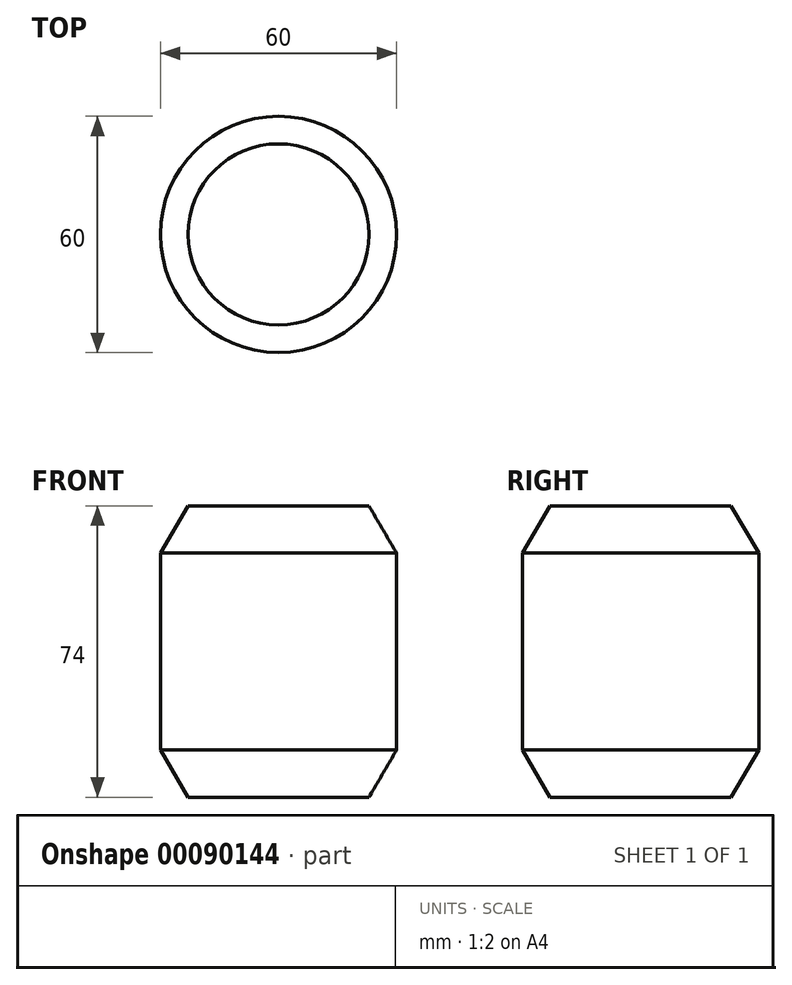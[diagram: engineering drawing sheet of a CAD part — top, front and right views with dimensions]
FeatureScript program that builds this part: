
annotation { "Feature Type Name" : "Feature", "Feature Type Description" : "" }
export const myFeature = defineFeature(function(context is Context, id is Id, definition is map)
    precondition{}
    {
        {
            var Q0;
            Q0=qCreatedBy(makeId("Top.planeOp"),FACE);
            var sketch = newSketch(context, id + "F0", { "sketchPlane" : qUnion([Q0])});
            skCircle(sketch, "E0", {"center": v(0, 0) * mm, "radius": 30 * mm});
            skCircle(sketch, "E1", {"center": v(0, 0) * mm, "radius": 23 * mm});
            skSolve(sketch);
        }
        {
            var Q0;
            Q0=makeQuery(id+"F0.imprint","IMPRINT",FACE,{"disambiguationData":[TD([[makeQuery(id+"F0.imprint","IMPRINT",EDGE,{"derivedFrom":sQuery(id+"F0.wireOp",EDGE,"E1")}),1.0]])]});
            var Q1;
            Q1=makeQuery(id+"F0.imprint","IMPRINT",FACE,{"disambiguationData":[TD([[makeQuery(id+"F0.imprint","IMPRINT",EDGE,{"derivedFrom":sQuery(id+"F0.wireOp",EDGE,"E0")}),1.0]])]});
            extrude(context, id + "F1", {"entities" : qUnion([Q0, Q1]), "depth" : 74 * mm});
        }
        {
            var Q0;
            Q0=makeQuery(id+"F1.opExtrude","CAP_EDGE",EDGE,{"disambiguationData":[OSD([sQuery(id+"F0.wireOp",EDGE,"E0")])],"isStart":false});
            var Q1;
            Q1=makeQuery(id+"F1.opExtrude","CAP_EDGE",EDGE,{"disambiguationData":[OSD([sQuery(id+"F0.wireOp",EDGE,"E0")])],"isStart":true});
            chamfer(context, id + "F2", {"entities" : qUnion([Q0, Q1]), "chamferType" : ChamferType.TWO_OFFSETS, "width1" : 7 * mm, "oppositeDirection" : false, "width2" : 12 * mm, "tangentPropagation" : true});
        }
    });
